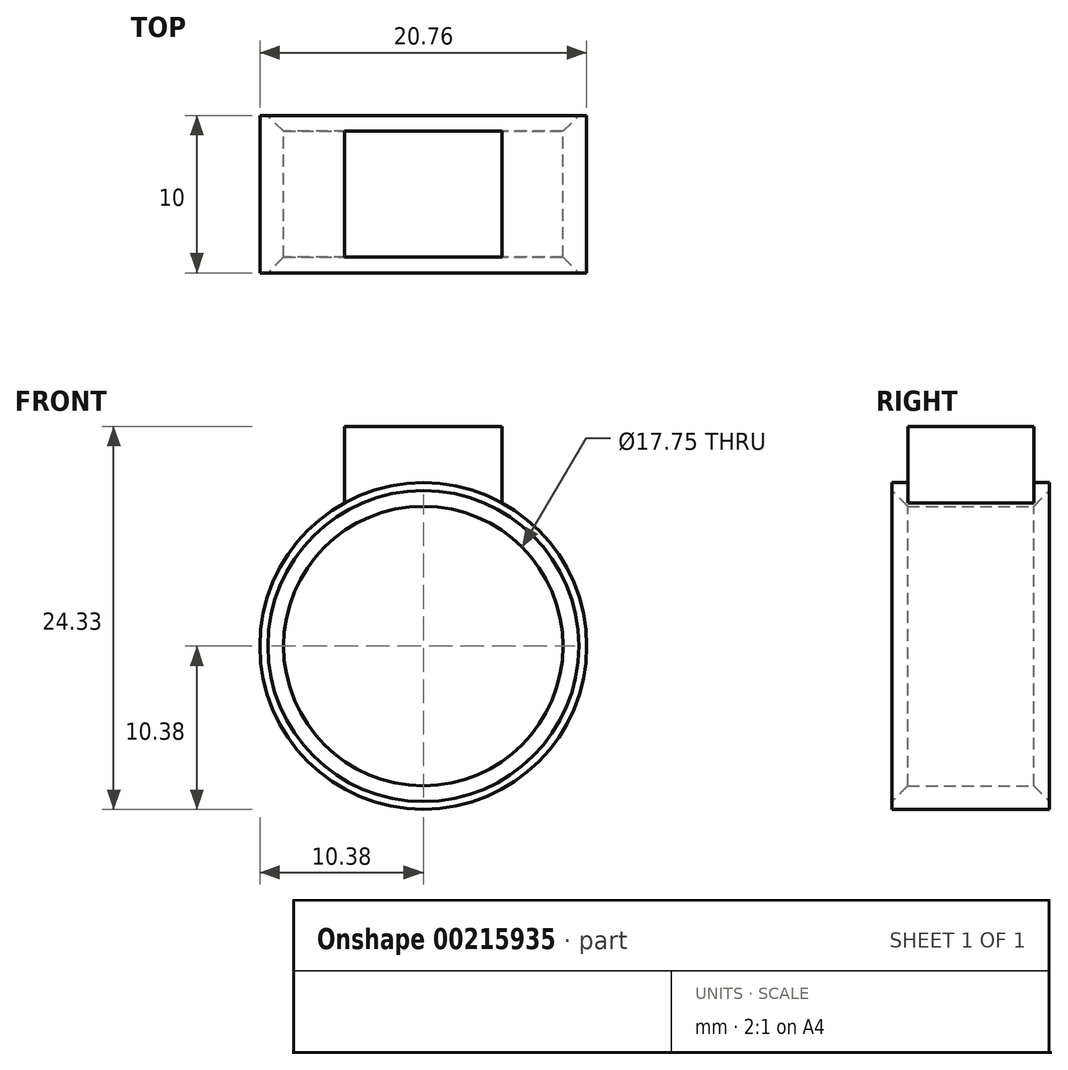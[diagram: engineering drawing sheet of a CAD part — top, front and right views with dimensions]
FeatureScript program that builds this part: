
annotation { "Feature Type Name" : "Feature", "Feature Type Description" : "" }
export const myFeature = defineFeature(function(context is Context, id is Id, definition is map)
    precondition{}
    {
        {
            var Q0;
            Q0=qCreatedBy(makeId("Front.planeOp"),FACE);
            var sketch = newSketch(context, id + "F0", { "sketchPlane" : qUnion([Q0])});
            skCircle(sketch, "E0", {"center": v(0, 0) * mm, "radius": 8.88 * mm});
            skCircle(sketch, "E1.0", {"center": v(0, 0) * mm, "radius": 10.38 * mm});
            skLineSegment(sketch, "E2.bottom", {"start": v(5, 8.95) * mm, "end": v(-5, 8.95) * mm});
            skLineSegment(sketch, "E2.top", {"start": v(5, 13.95) * mm, "end": v(-5, 13.95) * mm});
            skLineSegment(sketch, "E2.left", {"start": v(5, 8.95) * mm, "end": v(5, 13.95) * mm});
            skLineSegment(sketch, "E2.right", {"start": v(-5, 8.95) * mm, "end": v(-5, 13.95) * mm});
            skPoint(sketch, "E2.middle", {"position": v(0, 11.45) * mm});
            skSolve(sketch);
        }
        {
            var Q0;
            {var subQ0=sQuery(id+"F0.wireOp",EDGE,"E2.bottom");var subQ1=sQuery(id+"F0.wireOp",EDGE,"E1.0");var subQ2=makeQuery(id+"F0.imprint","INTERSECT",VERTEX,{"disambiguationData":[OD(0.0)],"derivedFrom":[subQ1,subQ0]});Q0=makeQuery(id+"F0.imprint","IMPRINT",FACE,{"disambiguationData":[TD([[makeQuery(id+"F0.imprint","IMPRINT",EDGE,{"disambiguationData":[TD([[subQ2,-1.0]])],"derivedFrom":subQ1}),1.0]])]});}
            var Q1;
            Q1=makeQuery(id+"F0.imprint","IMPRINT",FACE,{"disambiguationData":[TD([[makeQuery(id+"F0.imprint","IMPRINT",EDGE,{"derivedFrom":sQuery(id+"F0.wireOp",EDGE,"E0")}),-1.0]])]});
            extrude(context, id + "F1", {"entities" : qUnion([Q0, Q1]), "depth" : 5 * mm, "hasSecondDirection" : true, "secondDirectionOppositeDirection" : true, "secondDirectionDepth" : 5 * mm});
        }
        {
            var Q0;
            Q0=makeQuery(id+"F0.imprint","IMPRINT",FACE,{"disambiguationData":[TD([[makeQuery(id+"F0.imprint","IMPRINT",EDGE,{"derivedFrom":sQuery(id+"F0.wireOp",EDGE,"E2.top")}),1.0]])]});
            var Q1;
            {var subQ0=sQuery(id+"F0.wireOp",EDGE,"E2.bottom");var subQ1=sQuery(id+"F0.wireOp",EDGE,"E1.0");var subQ2=makeQuery(id+"F0.imprint","INTERSECT",VERTEX,{"disambiguationData":[OD(0.0)],"derivedFrom":[subQ1,subQ0]});Q1=makeQuery(id+"F0.imprint","IMPRINT",FACE,{"disambiguationData":[TD([[makeQuery(id+"F0.imprint","IMPRINT",EDGE,{"disambiguationData":[TD([[subQ2,-1.0]])],"derivedFrom":subQ1}),1.0]])]});}
            extrude(context, id + "F2", {"entities" : qUnion([Q0, Q1]), "operationType" : NewBodyOperationType.ADD, "depth" : 4 * mm, "hasSecondDirection" : true, "secondDirectionOppositeDirection" : true, "secondDirectionDepth" : 4 * mm});
        }
        {
            var Q0;
            Q0=makeQuery(id+"F1.opExtrude","CAP_EDGE",EDGE,{"disambiguationData":[OSD([sQuery(id+"F0.wireOp",EDGE,"E0")])],"isStart":true});
            var Q1;
            Q1=makeQuery(id+"F1.opExtrude","CAP_EDGE",EDGE,{"disambiguationData":[OSD([sQuery(id+"F0.wireOp",EDGE,"E0")])],"isStart":false});
            chamfer(context, id + "F3", {"entities" : qUnion([Q0, Q1]), "width" : 1 * mm, "tangentPropagation" : true});
        }
    });
